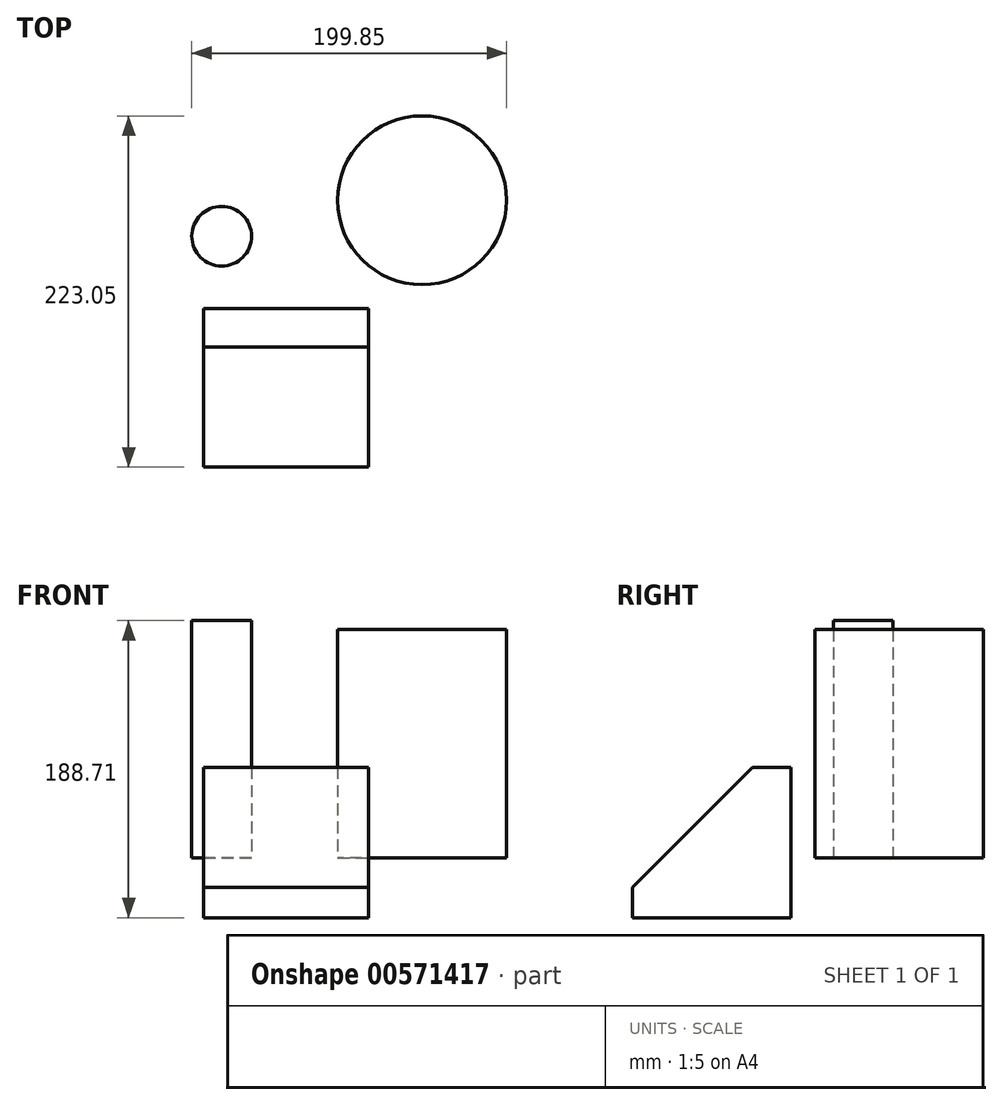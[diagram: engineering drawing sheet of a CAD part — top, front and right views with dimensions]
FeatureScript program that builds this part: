
annotation { "Feature Type Name" : "Feature", "Feature Type Description" : "" }
export const myFeature = defineFeature(function(context is Context, id is Id, definition is map)
    precondition{}
    {
        {
            var Q0;
            Q0=qCreatedBy(makeId("Front.planeOp"),FACE);
            var sketch = newSketch(context, id + "F0", { "sketchPlane" : qUnion([Q0])});
            skLineSegment(sketch, "E0.bottom", {"start": v(-51.5, 57.48) * mm, "end": v(53.18, 57.48) * mm});
            skLineSegment(sketch, "E0.top", {"start": v(-51.5, -38.07) * mm, "end": v(53.18, -38.07) * mm});
            skLineSegment(sketch, "E0.left", {"start": v(-51.5, 57.48) * mm, "end": v(-51.5, -38.07) * mm});
            skLineSegment(sketch, "E0.right", {"start": v(53.18, 57.48) * mm, "end": v(53.18, -38.07) * mm});
            skSolve(sketch);
        }
        {
            var Q0;
            Q0=makeQuery(id+"F0.imprint","IMPRINT",FACE,{"disambiguationData":[TD([[makeQuery(id+"F0.imprint","IMPRINT",EDGE,{"derivedFrom":sQuery(id+"F0.wireOp",EDGE,"E0.bottom")}),-1.0]])]});
            extrude(context, id + "F1", {"entities" : qUnion([Q0]), "depth" : 75.17 * mm, "offsetDistance" : 25.4 * mm, "hasSecondDirection" : true, "secondDirectionOppositeDirection" : true, "secondDirectionDepth" : 25.4 * mm});
        }
        {
            var Q0;
            Q0=makeQuery(id+"F1.opExtrude","CAP_EDGE",EDGE,{"disambiguationData":[OSD([sQuery(id+"F0.wireOp",EDGE,"E0.bottom")])],"isStart":false});
            chamfer(context, id + "F2", {"entities" : qUnion([Q0]), "width" : 76.2 * mm, "tangentPropagation" : true});
        }
        {
            var Q0;
            Q0=qCreatedBy(makeId("Top.planeOp"),FACE);
            var sketch = newSketch(context, id + "F3", { "sketchPlane" : qUnion([Q0])});
            skCircle(sketch, "E1", {"center": v(-40.16, 71.42) * mm, "radius": 18.95 * mm});
            skSolve(sketch);
        }
        {
            var Q0;
            Q0=makeQuery(id+"F3.imprint","IMPRINT",FACE,{"disambiguationData":[TD([[makeQuery(id+"F3.imprint","IMPRINT",EDGE,{"derivedFrom":sQuery(id+"F3.wireOp",EDGE,"E1")}),1.0]])]});
            extrude(context, id + "F4", {"entities" : qUnion([Q0]), "depth" : 150.64 * mm, "offsetDistance" : 25.4 * mm});
        }
        {
            var Q0;
            Q0=qCreatedBy(makeId("Top.planeOp"),FACE);
            var sketch = newSketch(context, id + "F5", { "sketchPlane" : qUnion([Q0])});
            skCircle(sketch, "E2", {"center": v(87.1, 94.26) * mm, "radius": 53.63 * mm});
            skSolve(sketch);
        }
        {
            var Q0;
            Q0 = qSketchRegion(id + "F5", true);
            extrude(context, id + "F6", {"entities" : qUnion([Q0]), "depth" : 144.89 * mm, "offsetDistance" : 25.4 * mm});
        }
    });
